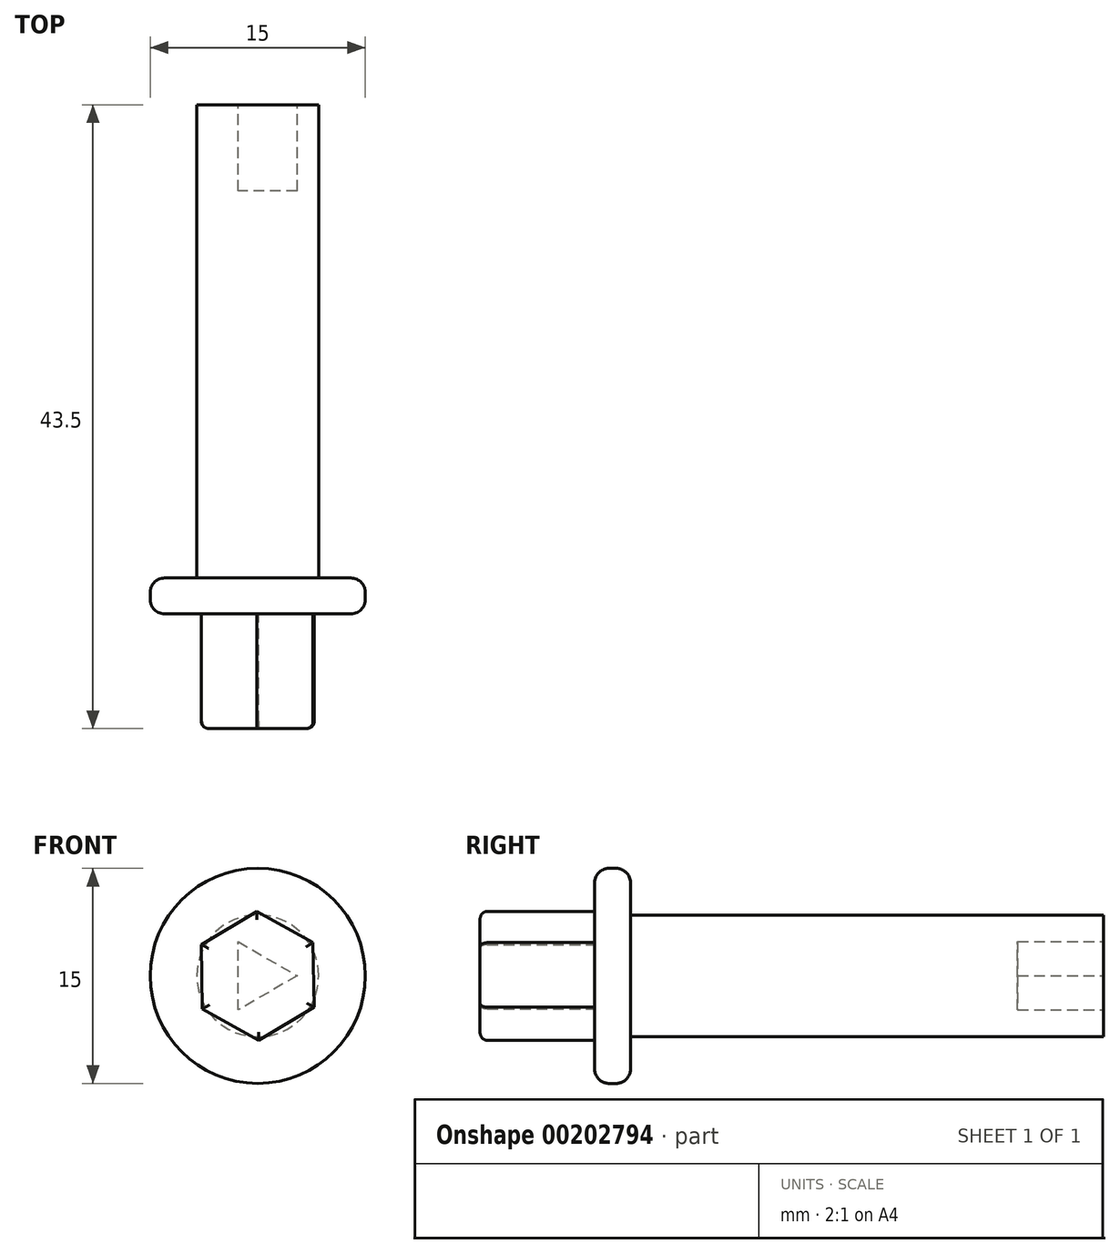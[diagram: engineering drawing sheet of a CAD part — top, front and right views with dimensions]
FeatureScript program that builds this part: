
annotation { "Feature Type Name" : "Feature", "Feature Type Description" : "" }
export const myFeature = defineFeature(function(context is Context, id is Id, definition is map)
    precondition{}
    {
        {
            var Q0;
            Q0=qCreatedBy(makeId("Front.planeOp"),FACE);
            var sketch = newSketch(context, id + "F0", { "sketchPlane" : qUnion([Q0])});
            skCircle(sketch, "E0", {"center": v(0, 0) * mm, "radius": 4.25 * mm});
            skCircle(sketch, "E1.0", {"center": v(0, 0) * mm, "radius": 2.75 * mm, "construction": true});
            skLineSegment(sketch, "E2.0", {"start": v(2.75, 0) * mm, "end": v(-1.38, -2.38) * mm});
            skLineSegment(sketch, "E2.1", {"start": v(-1.37, -2.38) * mm, "end": v(-1.37, 2.38) * mm});
            skLineSegment(sketch, "E2.2", {"start": v(-1.37, 2.38) * mm, "end": v(2.75, 0) * mm});
            skSolve(sketch);
        }
        {
            var Q0;
            Q0=makeQuery(id+"F0.imprint","IMPRINT",FACE,{"disambiguationData":[TD([[makeQuery(id+"F0.imprint","IMPRINT",EDGE,{"derivedFrom":sQuery(id+"F0.wireOp",EDGE,"E0")}),1.0]])]});
            var Q1;
            Q1=makeQuery(id+"F0.imprint","IMPRINT",FACE,{"disambiguationData":[TD([[makeQuery(id+"F0.imprint","IMPRINT",EDGE,{"derivedFrom":sQuery(id+"F0.wireOp",EDGE,"E2.0")}),-1.0]])]});
            extrude(context, id + "F1", {"entities" : qUnion([Q0, Q1]), "depth" : 33 * mm});
        }
        {
            var Q0;
            Q0=makeQuery(id+"F0.imprint","IMPRINT",FACE,{"disambiguationData":[TD([[makeQuery(id+"F0.imprint","IMPRINT",EDGE,{"derivedFrom":sQuery(id+"F0.wireOp",EDGE,"E2.0")}),-1.0]])]});
            extrude(context, id + "F2", {"entities" : qUnion([Q0]), "operationType" : NewBodyOperationType.REMOVE, "depth" : 6 * mm});
        }
        {
            var Q0;
            Q0=makeQuery(id+"F1.opExtrude","CAP_FACE",FACE,{"disambiguationData":[OSD([sQuery(id+"F0.wireOp",EDGE,"E0")])],"isStart":false});
            var sketch = newSketch(context, id + "F3", { "sketchPlane" : qUnion([Q0])});
            skCircle(sketch, "E3", {"center": v(0, 0) * mm, "radius": 7.5 * mm});
            skSolve(sketch);
        }
        {
            var Q0;
            Q0=makeQuery(id+"F3.imprint","IMPRINT",FACE,{"disambiguationData":[TD([[makeQuery(id+"F3.imprint","IMPRINT",EDGE,{"derivedFrom":sQuery(id+"F3.wireOp",EDGE,"E3")}),1.0]])]});
            var Q1;
            Q1=makeQuery(id+"F3.imprint","IMPRINT",FACE,{"disambiguationData":[TD([[makeQuery(id+"F3.imprint","IMPRINT",EDGE,{"derivedFrom":makeQuery(id+"F1.opExtrude","CAP_EDGE",EDGE,{"disambiguationData":[OSD([sQuery(id+"F0.wireOp",EDGE,"E0")])],"isStart":false})}),1.0]])]});
            extrude(context, id + "F4", {"entities" : qUnion([Q0, Q1]), "operationType" : NewBodyOperationType.ADD, "depth" : 2.5 * mm});
        }
        {
            var Q0;
            Q0=makeQuery(id+"F4.opExtrude","CAP_FACE",FACE,{"disambiguationData":[OSD([sQuery(id+"F3.wireOp",EDGE,"E3")])],"isStart":false});
            var sketch = newSketch(context, id + "F5", { "sketchPlane" : qUnion([Q0])});
            skCircle(sketch, "E4", {"center": v(0, 0) * mm, "radius": 4.5 * mm, "construction": true});
            skLineSegment(sketch, "E5.0", {"start": v(3.93, -2.18) * mm, "end": v(0.08, -4.5) * mm});
            skLineSegment(sketch, "E5.1", {"start": v(0.08, -4.5) * mm, "end": v(-3.86, -2.32) * mm});
            skLineSegment(sketch, "E5.2", {"start": v(-3.86, -2.32) * mm, "end": v(-3.93, 2.18) * mm});
            skLineSegment(sketch, "E5.3", {"start": v(-3.93, 2.18) * mm, "end": v(-0.08, 4.5) * mm});
            skLineSegment(sketch, "E5.4", {"start": v(-0.08, 4.5) * mm, "end": v(3.86, 2.32) * mm});
            skLineSegment(sketch, "E5.5", {"start": v(3.86, 2.32) * mm, "end": v(3.93, -2.18) * mm});
            skSolve(sketch);
        }
        {
            var Q0;
            Q0=makeQuery(id+"F5.imprint","IMPRINT",FACE,{"disambiguationData":[TD([[makeQuery(id+"F5.imprint","IMPRINT",EDGE,{"derivedFrom":sQuery(id+"F5.wireOp",EDGE,"E5.0")}),-1.0]])]});
            extrude(context, id + "F6", {"entities" : qUnion([Q0]), "operationType" : NewBodyOperationType.ADD, "depth" : 8 * mm});
        }
        {
            var Q0;
            Q0=makeQuery(id+"F6.opExtrude","CAP_EDGE",EDGE,{"disambiguationData":[OSD([sQuery(id+"F5.wireOp",EDGE,"E5.0")])],"isStart":false});
            var Q1;
            Q1=makeQuery(id+"F6.opExtrude","CAP_EDGE",EDGE,{"disambiguationData":[OSD([sQuery(id+"F5.wireOp",EDGE,"E5.1")])],"isStart":false});
            var Q2;
            Q2=makeQuery(id+"F6.opExtrude","CAP_EDGE",EDGE,{"disambiguationData":[OSD([sQuery(id+"F5.wireOp",EDGE,"E5.2")])],"isStart":false});
            var Q3;
            Q3=makeQuery(id+"F6.opExtrude","CAP_EDGE",EDGE,{"disambiguationData":[OSD([sQuery(id+"F5.wireOp",EDGE,"E5.3")])],"isStart":false});
            var Q4;
            Q4=makeQuery(id+"F6.opExtrude","CAP_EDGE",EDGE,{"disambiguationData":[OSD([sQuery(id+"F5.wireOp",EDGE,"E5.4")])],"isStart":false});
            var Q5;
            Q5=makeQuery(id+"F6.opExtrude","CAP_EDGE",EDGE,{"disambiguationData":[OSD([sQuery(id+"F5.wireOp",EDGE,"E5.5")])],"isStart":false});
            fillet(context, id + "F7", {"entities" : qUnion([Q0, Q1, Q2, Q3, Q4, Q5]), "radius" : .5 * mm, "tangentPropagation" : true, "allowEdgeOverflow" : false});
        }
        {
            var Q0;
            Q0=makeQuery(id+"F4.opExtrude","CAP_EDGE",EDGE,{"disambiguationData":[OSD([sQuery(id+"F3.wireOp",EDGE,"E3")])],"isStart":false});
            var Q1;
            Q1=makeQuery(id+"F4.opExtrude","CAP_EDGE",EDGE,{"disambiguationData":[OSD([sQuery(id+"F3.wireOp",EDGE,"E3")])],"isStart":true});
            fillet(context, id + "F8", {"entities" : qUnion([Q0, Q1]), "radius" : 1 * mm, "tangentPropagation" : true, "allowEdgeOverflow" : false});
        }
    });
